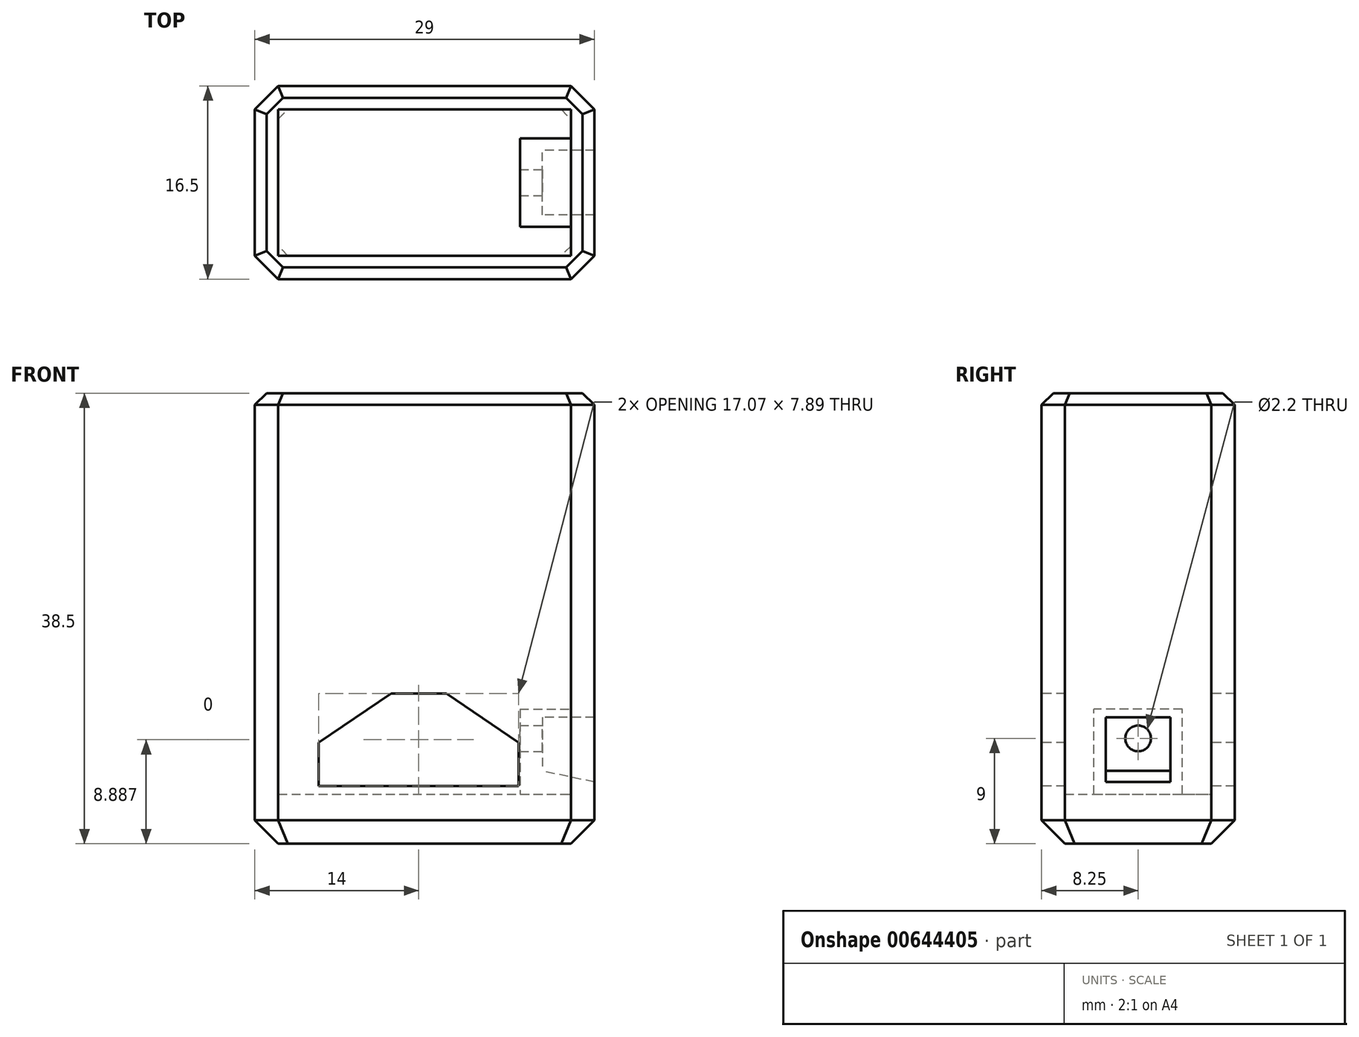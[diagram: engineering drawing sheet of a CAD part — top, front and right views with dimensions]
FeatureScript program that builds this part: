
annotation { "Feature Type Name" : "Feature", "Feature Type Description" : "" }
export const myFeature = defineFeature(function(context is Context, id is Id, definition is map)
    precondition{}
    {
        {
            var Q0;
            Q0=qCreatedBy(makeId("Top.planeOp"),FACE);
            var sketch = newSketch(context, id + "F0", { "sketchPlane" : qUnion([Q0])});
            skLineSegment(sketch, "E0.bottom", {"start": v(0, 0) * mm, "end": v(29, 0) * mm});
            skLineSegment(sketch, "E0.top", {"start": v(0, 16.5) * mm, "end": v(29, 16.5) * mm});
            skLineSegment(sketch, "E0.left", {"start": v(0, 0) * mm, "end": v(0, 16.5) * mm});
            skLineSegment(sketch, "E0.right", {"start": v(29, 0) * mm, "end": v(29, 16.5) * mm});
            skSolve(sketch);
        }
        {
            var Q0;
            Q0=makeQuery(id+"F0.imprint","IMPRINT",FACE,{"disambiguationData":[TD([[makeQuery(id+"F0.imprint","IMPRINT",EDGE,{"derivedFrom":sQuery(id+"F0.wireOp",EDGE,"E0.bottom")}),1.0]])]});
            extrude(context, id + "F1", {"entities" : qUnion([Q0]), "depth" : 38.5 * mm, "offsetDistance" : 25 * mm});
        }
        {
            var Q0;
            Q0=makeQuery(id+"F1.opExtrude","CAP_FACE",FACE,{"disambiguationData":[OSD([sQuery(id+"F0.wireOp",EDGE,"E0.bottom"),sQuery(id+"F0.wireOp",EDGE,"E0.top"),sQuery(id+"F0.wireOp",EDGE,"E0.left"),sQuery(id+"F0.wireOp",EDGE,"E0.right")])],"isStart":false});
            shell(context, id + "F2", {"entities" : qUnion([Q0]), "thickness" : 2 * mm});
        }
        {
            var Q0;
            Q0=makeQuery(id+"F2.opShell","OFFSET_FACE",FACE,{"disambiguationData":[OSD([sQuery(id+"F0.wireOp",EDGE,"E0.bottom"),sQuery(id+"F0.wireOp",EDGE,"E0.top"),sQuery(id+"F0.wireOp",EDGE,"E0.left"),sQuery(id+"F0.wireOp",EDGE,"E0.right")])]});
            extrude(context, id + "F3", {"entities" : qUnion([Q0]), "operationType" : NewBodyOperationType.ADD, "depth" : 2.25 * mm, "offsetDistance" : 25 * mm});
        }
        {
            var Q0;
            Q0=makeQuery(id+"F1.opExtrude","SWEPT_EDGE",EDGE,{"disambiguationData":[OSD([sQuery(id+"F0.wireOp",EDGE,"E0.bottom"),sQuery(id+"F0.wireOp",EDGE,"E0.right")])]});
            var Q1;
            Q1=makeQuery(id+"F1.opExtrude","SWEPT_EDGE",EDGE,{"disambiguationData":[OSD([sQuery(id+"F0.wireOp",EDGE,"E0.top"),sQuery(id+"F0.wireOp",EDGE,"E0.right")])]});
            var Q2;
            Q2=makeQuery(id+"F1.opExtrude","SWEPT_EDGE",EDGE,{"disambiguationData":[OSD([sQuery(id+"F0.wireOp",EDGE,"E0.bottom"),sQuery(id+"F0.wireOp",EDGE,"E0.left")])]});
            var Q3;
            Q3=makeQuery(id+"F1.opExtrude","SWEPT_EDGE",EDGE,{"disambiguationData":[OSD([sQuery(id+"F0.wireOp",EDGE,"E0.top"),sQuery(id+"F0.wireOp",EDGE,"E0.left")])]});
            chamfer(context, id + "F4", {"entities" : qUnion([Q0, Q1, Q2, Q3]), "width" : 2 * mm, "tangentPropagation" : true});
        }
        {
            var Q0;
            Q0=makeQuery(id+"F1.opExtrude","CAP_FACE",FACE,{"disambiguationData":[OSD([sQuery(id+"F0.wireOp",EDGE,"E0.bottom"),sQuery(id+"F0.wireOp",EDGE,"E0.top"),sQuery(id+"F0.wireOp",EDGE,"E0.left"),sQuery(id+"F0.wireOp",EDGE,"E0.right")])],"isStart":true});
            chamfer(context, id + "F5", {"entities" : qUnion([Q0]), "width" : 2 * mm, "tangentPropagation" : true});
        }
        {
            var Q0;
            Q0=makeQuery(id+"F1.opExtrude","CAP_EDGE",EDGE,{"disambiguationData":[OSD([sQuery(id+"F0.wireOp",EDGE,"E0.top")])],"isStart":false});
            var Q1;
            {var subQ0=sQuery(id+"F0.wireOp",EDGE,"E0.left");var subQ1=sQuery(id+"F0.wireOp",EDGE,"E0.top");Q1=makeQuery(id+"F4.opChamfer","BLEND_EDGE",EDGE,{"blendedFrom":[makeQuery(id+"F1.opExtrude","SWEPT_EDGE",EDGE,{"disambiguationData":[OSD([subQ1,subQ0])]}),makeQuery(id+"F1.opExtrude","CAP_FACE",FACE,{"disambiguationData":[OSD([sQuery(id+"F0.wireOp",EDGE,"E0.bottom"),subQ1,subQ0,sQuery(id+"F0.wireOp",EDGE,"E0.right")])],"isStart":false})],"blendedInto":[makeQuery(id+"F1.opExtrude","CAP_FACE",FACE,{"disambiguationData":[OSD([sQuery(id+"F0.wireOp",EDGE,"E0.bottom"),subQ1,subQ0,sQuery(id+"F0.wireOp",EDGE,"E0.right")])],"isStart":false})]});}
            var Q2;
            Q2=makeQuery(id+"F1.opExtrude","CAP_EDGE",EDGE,{"disambiguationData":[OSD([sQuery(id+"F0.wireOp",EDGE,"E0.left")])],"isStart":false});
            var Q3;
            {var subQ0=sQuery(id+"F0.wireOp",EDGE,"E0.left");var subQ1=sQuery(id+"F0.wireOp",EDGE,"E0.bottom");Q3=makeQuery(id+"F4.opChamfer","BLEND_EDGE",EDGE,{"blendedFrom":[makeQuery(id+"F1.opExtrude","SWEPT_EDGE",EDGE,{"disambiguationData":[OSD([subQ1,subQ0])]}),makeQuery(id+"F1.opExtrude","CAP_FACE",FACE,{"disambiguationData":[OSD([subQ1,sQuery(id+"F0.wireOp",EDGE,"E0.top"),subQ0,sQuery(id+"F0.wireOp",EDGE,"E0.right")])],"isStart":false})],"blendedInto":[makeQuery(id+"F1.opExtrude","CAP_FACE",FACE,{"disambiguationData":[OSD([subQ1,sQuery(id+"F0.wireOp",EDGE,"E0.top"),subQ0,sQuery(id+"F0.wireOp",EDGE,"E0.right")])],"isStart":false})]});}
            var Q4;
            Q4=makeQuery(id+"F1.opExtrude","CAP_EDGE",EDGE,{"disambiguationData":[OSD([sQuery(id+"F0.wireOp",EDGE,"E0.bottom")])],"isStart":false});
            var Q5;
            {var subQ0=sQuery(id+"F0.wireOp",EDGE,"E0.right");var subQ1=sQuery(id+"F0.wireOp",EDGE,"E0.bottom");Q5=makeQuery(id+"F4.opChamfer","BLEND_EDGE",EDGE,{"blendedFrom":[makeQuery(id+"F1.opExtrude","SWEPT_EDGE",EDGE,{"disambiguationData":[OSD([subQ1,subQ0])]}),makeQuery(id+"F1.opExtrude","CAP_FACE",FACE,{"disambiguationData":[OSD([subQ1,sQuery(id+"F0.wireOp",EDGE,"E0.top"),sQuery(id+"F0.wireOp",EDGE,"E0.left"),subQ0])],"isStart":false})],"blendedInto":[makeQuery(id+"F1.opExtrude","CAP_FACE",FACE,{"disambiguationData":[OSD([subQ1,sQuery(id+"F0.wireOp",EDGE,"E0.top"),sQuery(id+"F0.wireOp",EDGE,"E0.left"),subQ0])],"isStart":false})]});}
            var Q6;
            Q6=makeQuery(id+"F1.opExtrude","CAP_EDGE",EDGE,{"disambiguationData":[OSD([sQuery(id+"F0.wireOp",EDGE,"E0.right")])],"isStart":false});
            var Q7;
            {var subQ0=sQuery(id+"F0.wireOp",EDGE,"E0.right");var subQ1=sQuery(id+"F0.wireOp",EDGE,"E0.top");Q7=makeQuery(id+"F4.opChamfer","BLEND_EDGE",EDGE,{"blendedFrom":[makeQuery(id+"F1.opExtrude","SWEPT_EDGE",EDGE,{"disambiguationData":[OSD([subQ1,subQ0])]}),makeQuery(id+"F1.opExtrude","CAP_FACE",FACE,{"disambiguationData":[OSD([sQuery(id+"F0.wireOp",EDGE,"E0.bottom"),subQ1,sQuery(id+"F0.wireOp",EDGE,"E0.left"),subQ0])],"isStart":false})],"blendedInto":[makeQuery(id+"F1.opExtrude","CAP_FACE",FACE,{"disambiguationData":[OSD([sQuery(id+"F0.wireOp",EDGE,"E0.bottom"),subQ1,sQuery(id+"F0.wireOp",EDGE,"E0.left"),subQ0])],"isStart":false})]});}
            chamfer(context, id + "F6", {"entities" : qUnion([Q0, Q1, Q2, Q3, Q4, Q5, Q6, Q7]), "width" : 1 * mm, "tangentPropagation" : true});
        }
        {
            var Q0;
            Q0=makeQuery(id+"F1.opExtrude","SWEPT_FACE",FACE,{"disambiguationData":[OSD([sQuery(id+"F0.wireOp",EDGE,"E0.bottom")])]});
            var sketch = newSketch(context, id + "F7", { "sketchPlane" : qUnion([Q0])});
            skLineSegment(sketch, "E1", {"start": v(22.54, 4.94) * mm, "end": v(5.46, 4.94) * mm});
            skLineSegment(sketch, "E2", {"start": v(5.46, 4.94) * mm, "end": v(5.46, 8.66) * mm});
            skLineSegment(sketch, "E3", {"start": v(5.46, 8.66) * mm, "end": v(11.63, 12.83) * mm});
            skLineSegment(sketch, "E4", {"start": v(11.63, 12.83) * mm, "end": v(16.37, 12.83) * mm});
            skLineSegment(sketch, "E5", {"start": v(16.37, 12.83) * mm, "end": v(22.54, 8.66) * mm});
            skLineSegment(sketch, "E6", {"start": v(22.54, 8.66) * mm, "end": v(22.54, 4.94) * mm});
            skSolve(sketch);
        }
        {
            var Q0;
            Q0=makeQuery(id+"F7.imprint","IMPRINT",FACE,{"disambiguationData":[TD([[makeQuery(id+"F7.imprint","IMPRINT",EDGE,{"derivedFrom":sQuery(id+"F7.wireOp",EDGE,"E1")}),-1.0]])]});
            extrude(context, id + "F8", {"entities" : qUnion([Q0]), "operationType" : NewBodyOperationType.REMOVE, "endBound" : BoundingType.THROUGH_ALL, "oppositeDirection" : true, "depth" : 25 * mm, "offsetDistance" : 25 * mm});
        }
        {
            var Q0;
            Q0=makeQuery(id+"F1.opExtrude","SWEPT_FACE",FACE,{"disambiguationData":[OSD([sQuery(id+"F0.wireOp",EDGE,"E0.right")])]});
            var sketch = newSketch(context, id + "F9", { "sketchPlane" : qUnion([Q0])});
            skLineSegment(sketch, "E7.bottom", {"start": v(4.48, 11.5) * mm, "end": v(12.02, 11.5) * mm});
            skLineSegment(sketch, "E7.top", {"start": v(4.48, 4.25) * mm, "end": v(12.02, 4.25) * mm});
            skLineSegment(sketch, "E7.left", {"start": v(4.48, 11.5) * mm, "end": v(4.48, 4.25) * mm});
            skLineSegment(sketch, "E7.right", {"start": v(12.02, 11.5) * mm, "end": v(12.02, 4.25) * mm});
            skCircle(sketch, "E8", {"center": v(8.25, 9) * mm, "radius": 1.1 * mm});
            skSolve(sketch);
        }
        {
            var Q0;
            Q0=makeQuery(id+"F9.imprint","IMPRINT",FACE,{"disambiguationData":[TD([[makeQuery(id+"F9.imprint","IMPRINT",EDGE,{"derivedFrom":sQuery(id+"F9.wireOp",EDGE,"E7.bottom")}),-1.0]])]});
            extrude(context, id + "F10", {"entities" : qUnion([Q0]), "operationType" : NewBodyOperationType.ADD, "oppositeDirection" : true, "depth" : 6.35 * mm, "offsetDistance" : 25 * mm});
        }
        {
            var Q0;
            Q0=makeQuery(id+"F1.opExtrude","SWEPT_FACE",FACE,{"disambiguationData":[OSD([sQuery(id+"F0.wireOp",EDGE,"E0.right")])]});
            var sketch = newSketch(context, id + "F11", { "sketchPlane" : qUnion([Q0])});
            skLineSegment(sketch, "E9.bottom", {"start": v(5.48, 10.8) * mm, "end": v(11.02, 10.8) * mm});
            skLineSegment(sketch, "E9.top", {"start": v(5.48, 5.27) * mm, "end": v(11.02, 5.27) * mm});
            skLineSegment(sketch, "E9.left", {"start": v(5.48, 10.8) * mm, "end": v(5.48, 5.27) * mm});
            skLineSegment(sketch, "E9.right", {"start": v(11.02, 10.8) * mm, "end": v(11.02, 5.27) * mm});
            skSolve(sketch);
        }
        {
            var Q0;
            Q0=makeQuery(id+"F11.imprint","IMPRINT",FACE,{"disambiguationData":[TD([[makeQuery(id+"F11.imprint","IMPRINT",EDGE,{"derivedFrom":sQuery(id+"F11.wireOp",EDGE,"E9.bottom")}),1.0]])]});
            cPlane(context, id + "F12", {"entities" : qUnion([Q0]), "cplaneType" : CPlaneType.OFFSET, "offset" : 4.45 * mm, "oppositeDirection" : true, "width" : 150 * mm, "height" : 150 * mm});
        }
        {
            var Q0;
            Q0=qCreatedBy(id+"F12.planeOp",FACE);
            var sketch = newSketch(context, id + "F13", { "sketchPlane" : qUnion([Q0])});
            skLineSegment(sketch, "E10.bottom", {"start": v(5.48, 10.8) * mm, "end": v(11.02, 10.8) * mm});
            skLineSegment(sketch, "E10.top", {"start": v(5.48, 6.22) * mm, "end": v(11.02, 6.22) * mm});
            skLineSegment(sketch, "E10.left", {"start": v(5.48, 10.8) * mm, "end": v(5.48, 6.22) * mm});
            skLineSegment(sketch, "E10.right", {"start": v(11.02, 10.8) * mm, "end": v(11.02, 6.22) * mm});
            skSolve(sketch);
        }
        {
            var Q1;
            Q1 = qSketchRegion(id + "F11", true);
            var Q2;
            Q2 = qSketchRegion(id + "F13", true);
            loft(context, id + "F14", {"operationType" : NewBodyOperationType.REMOVE, "sheetProfilesArray" : [{ "sheetProfileEntities" : qUnion([Q1]) }, { "sheetProfileEntities" : qUnion([Q2]) }]});
        }
    });
